# Revit family: FU_Modular_Sandler_Lin 1230
name_source: partatom
category: Furniture
units: mm (PartAtom-declared; Revit-internal decimal feet)

## family parameters
Always vertical = Yes
Cut with Voids When Loaded = No
OmniClass Number = 23.40.20.00
OmniClass Title = General Furniture and Specialties
Render Appearance Source = Family Geometry
Room Calculation Point = No
Shared = No
Work Plane-Based = No

## types (1)
- Lin 1230
    Default Elevation = 0 mm  [stored 0 ft]
    Depth = 558 mm
    Description = Intermediate leg for Lin Bench made of injected aluminum alloy.
Greenguard Gold-certified to protect indoor air quality.
    Height = 418 mm  [stored 1.37139 ft]
    Manufacturer = Sandler
    Model = Lin 1230
    URL = https://www.sandlerseating.com
    Width = 37 mm

note: [stored X ft] marks values corroborated as IEEE doubles in the binary element streams (Revit-internal decimal feet)

## geometry (parser evidence)
native form markers: Sweep x3
no freeform markers — native parametric forms only
